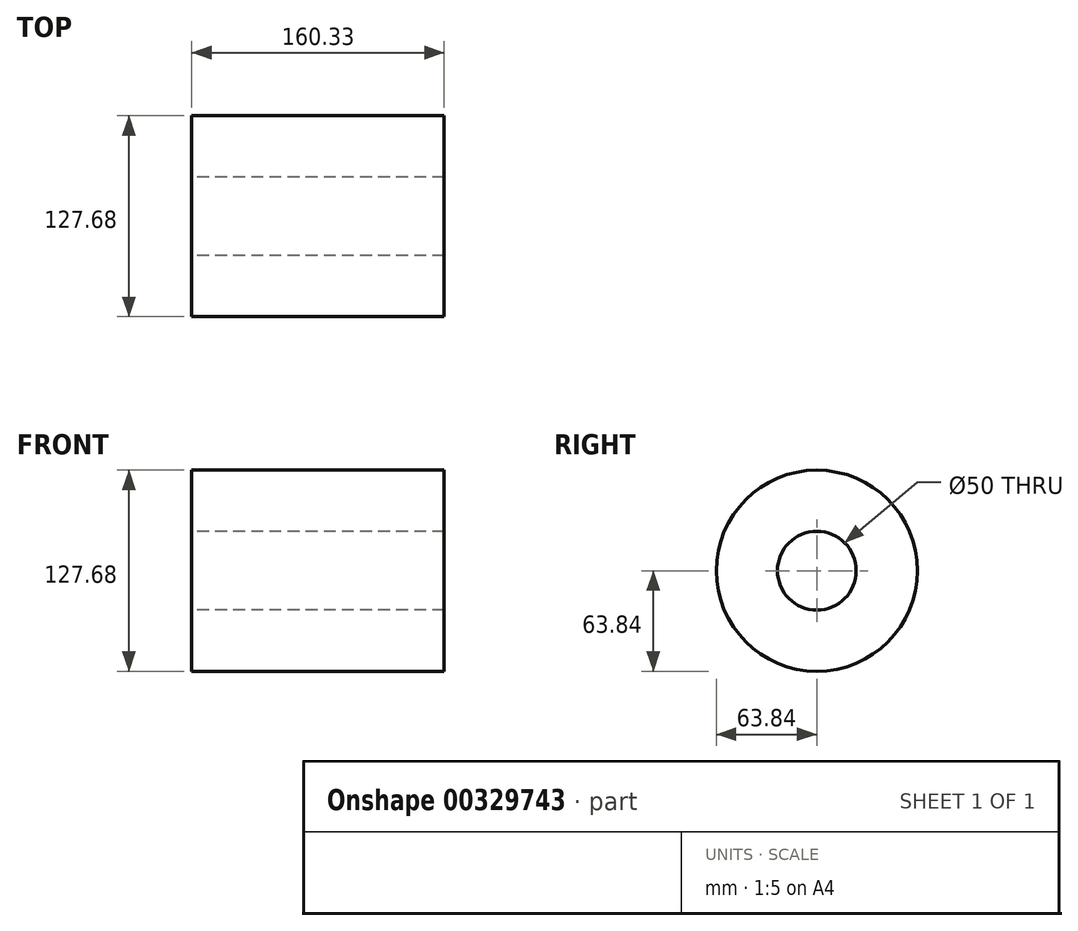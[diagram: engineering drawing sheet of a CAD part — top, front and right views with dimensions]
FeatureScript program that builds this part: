
annotation { "Feature Type Name" : "Feature", "Feature Type Description" : "" }
export const myFeature = defineFeature(function(context is Context, id is Id, definition is map)
    precondition{}
    {
        {
            var Q0;
            Q0=qCreatedBy(makeId("Front.planeOp"),FACE);
            var sketch = newSketch(context, id + "F0", { "sketchPlane" : qUnion([Q0])});
            skLineSegment(sketch, "E0", {"start": v(-66.12, 0) * mm, "end": v(133.06, 0) * mm, "construction": true});
            skLineSegment(sketch, "E1.bottom", {"start": v(-66.94, 63.84) * mm, "end": v(93.39, 63.84) * mm});
            skLineSegment(sketch, "E1.top", {"start": v(-66.94, 25) * mm, "end": v(93.39, 25) * mm});
            skLineSegment(sketch, "E1.left", {"start": v(-66.94, 63.84) * mm, "end": v(-66.94, 25) * mm});
            skLineSegment(sketch, "E1.right", {"start": v(93.39, 63.84) * mm, "end": v(93.39, 25) * mm});
            skSolve(sketch);
        }
        {
            var Q0;
            Q0=qSketchRegion(id+"F0",true);
            var Q1;
            Q1=sQuery(id+"F0.wireOp",EDGE,"E0");
            revolve(context, id + "F1", {"entities" : qUnion([Q0]), "axis" : qUnion([Q1]), "revolveType" : RevolveType.FULL});
        }
    });
